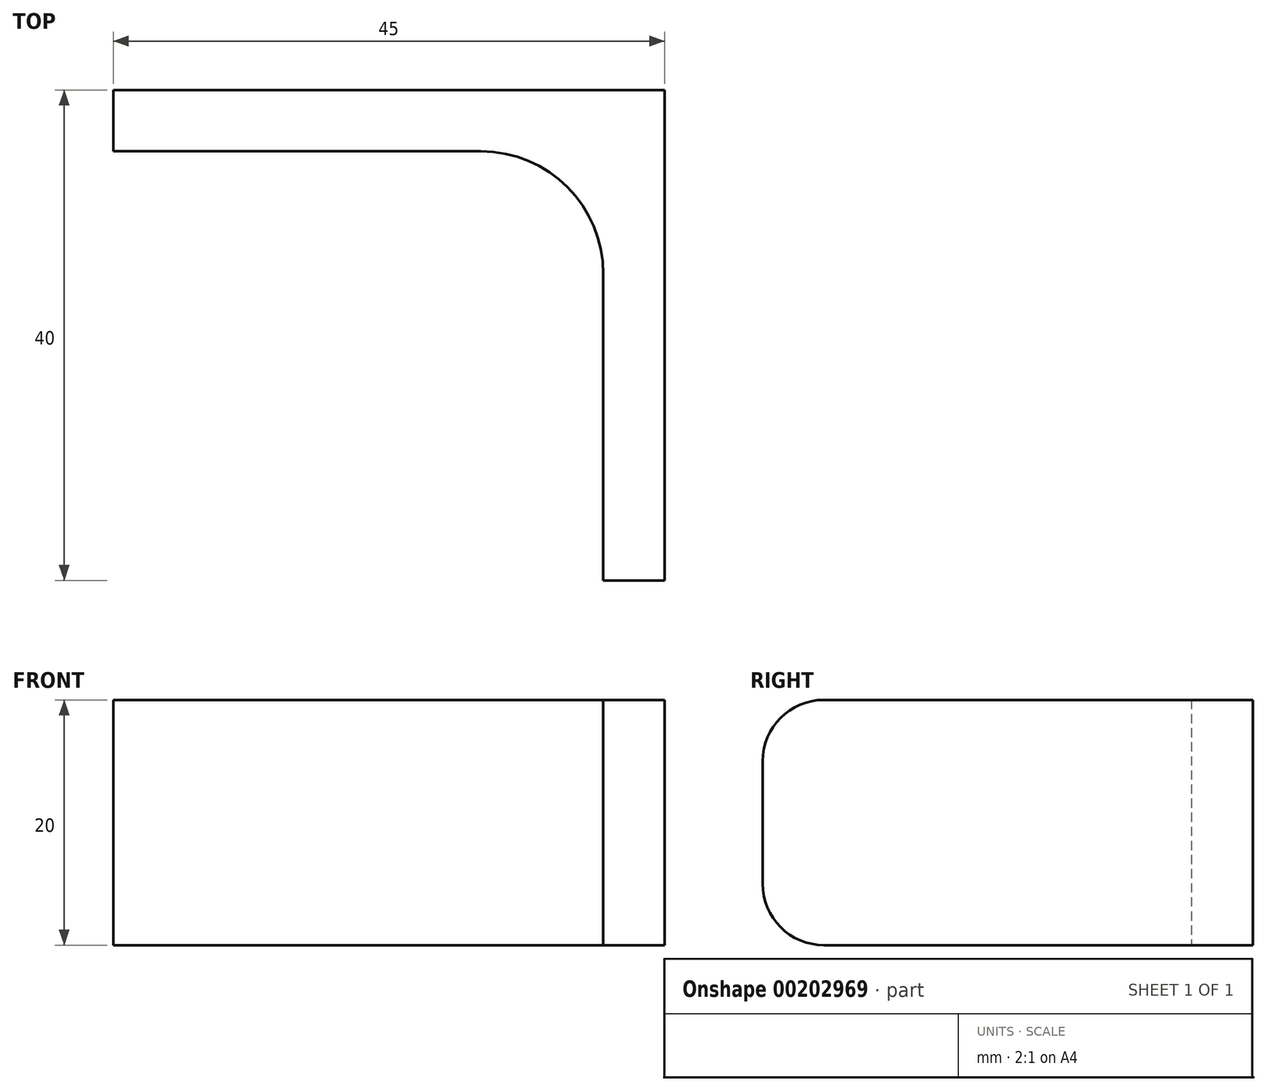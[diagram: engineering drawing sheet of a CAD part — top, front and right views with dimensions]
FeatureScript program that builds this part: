
annotation { "Feature Type Name" : "Feature", "Feature Type Description" : "" }
export const myFeature = defineFeature(function(context is Context, id is Id, definition is map)
    precondition{}
    {
        {
            var Q0;
            Q0=qCreatedBy(makeId("Top.planeOp"),FACE);
            var sketch = newSketch(context, id + "F0", { "sketchPlane" : qUnion([Q0])});
            skLineSegment(sketch, "E0", {"start": v(0, 0) * mm, "end": v(-22.5, 0) * mm});
            skLineSegment(sketch, "E1", {"start": v(-22.5, 0) * mm, "end": v(-22.5, -5) * mm});
            skLineSegment(sketch, "E2", {"start": v(-22.5, -5) * mm, "end": v(7.5, -5) * mm});
            skLineSegment(sketch, "E3", {"start": v(17.5, -15) * mm, "end": v(17.5, -40) * mm});
            skLineSegment(sketch, "E4", {"start": v(17.5, -40) * mm, "end": v(22.5, -40) * mm});
            skLineSegment(sketch, "E5", {"start": v(22.5, -40) * mm, "end": v(22.5, 0) * mm});
            skLineSegment(sketch, "E6", {"start": v(22.5, 0) * mm, "end": v(0, 0) * mm});
            skPoint(sketch, "E7.visualSharp", {"position": v(17.5, -5) * mm});
            skArc(sketch, "E7.filletArc", {"start": v(17.5, -15) * mm, "mid": v(14.57, -7.93) * mm, "end": v(7.5, -5) * mm});
            skPoint(sketch, "E8.visualSharp", {"position": v(22.5, -40) * mm});
            skLineSegment(sketch, "E8.filletArc", {"start": v(22.5, -40) * mm, "end": v(22.5, -40) * mm});
            skPoint(sketch, "E9.visualSharp", {"position": v(17.5, -40) * mm});
            skLineSegment(sketch, "E9.filletArc", {"start": v(17.5, -40) * mm, "end": v(17.5, -40) * mm});
            skPoint(sketch, "E10.visualSharp", {"position": v(-22.5, -5) * mm});
            skLineSegment(sketch, "E10.filletArc", {"start": v(-22.5, -5) * mm, "end": v(-22.5, -5) * mm});
            skSolve(sketch);
        }
        {
            var Q0;
            Q0=makeQuery(id+"F0.imprint","IMPRINT",FACE,{"disambiguationData":[TD([[makeQuery(id+"F0.imprint","IMPRINT",EDGE,{"derivedFrom":sQuery(id+"F0.wireOp",EDGE,"E0")}),1.0]])]});
            extrude(context, id + "F1", {"entities" : qUnion([Q0]), "depth" : 20 * mm});
        }
        {
            var Q0;
            Q0=makeQuery(id+"F1.opExtrude","CAP_EDGE",EDGE,{"disambiguationData":[OSD([sQuery(id+"F0.wireOp",EDGE,"E4")])],"isStart":false});
            var Q1;
            Q1=makeQuery(id+"F1.opExtrude","CAP_EDGE",EDGE,{"disambiguationData":[OSD([sQuery(id+"F0.wireOp",EDGE,"E4")])],"isStart":true});
            fillet(context, id + "F2", {"entities" : qUnion([Q0, Q1]), "radius" : 5 * mm, "tangentPropagation" : true, "allowEdgeOverflow" : false});
        }
    });
